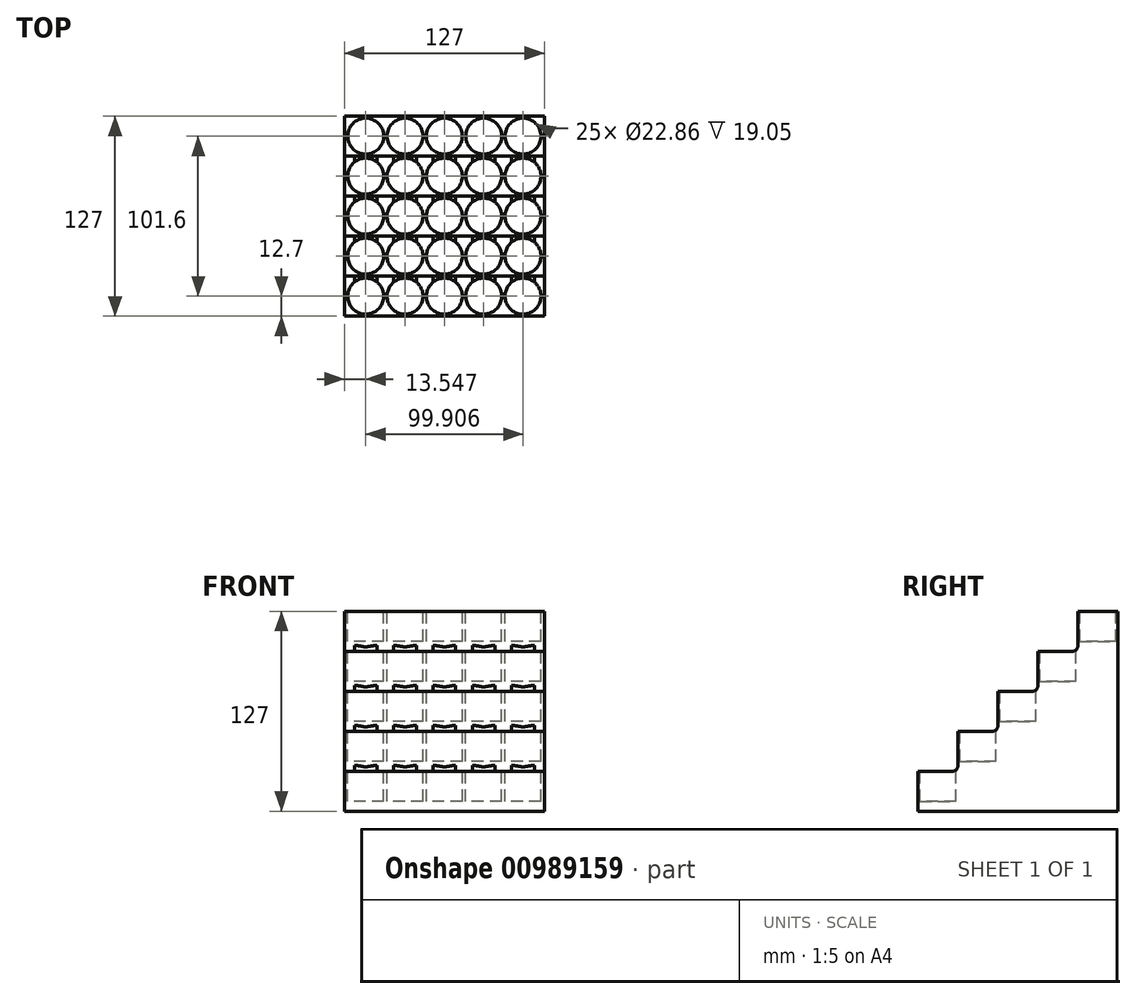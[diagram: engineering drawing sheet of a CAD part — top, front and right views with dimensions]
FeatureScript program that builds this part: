
annotation { "Feature Type Name" : "Feature", "Feature Type Description" : "" }
export const myFeature = defineFeature(function(context is Context, id is Id, definition is map)
    precondition{}
    {
        {
            var Q0;
            Q0=qCreatedBy(makeId("Top.planeOp"),FACE);
            var sketch = newSketch(context, id + "F0", { "sketchPlane" : qUnion([Q0])});
            skLineSegment(sketch, "E0.bottom", {"start": v(63.5, -63.5) * mm, "end": v(-63.5, -63.5) * mm});
            skLineSegment(sketch, "E0.top", {"start": v(63.5, 63.5) * mm, "end": v(-63.5, 63.5) * mm});
            skLineSegment(sketch, "E0.left", {"start": v(63.5, -63.5) * mm, "end": v(63.5, 63.5) * mm});
            skLineSegment(sketch, "E0.right", {"start": v(-63.5, -63.5) * mm, "end": v(-63.5, 63.5) * mm});
            skPoint(sketch, "E0.middle", {"position": v(0, 0) * mm});
            skSolve(sketch);
        }
        {
            var Q0;
            Q0=makeQuery(id+"F0.imprint","IMPRINT",FACE,{"disambiguationData":[TD([[makeQuery(id+"F0.imprint","IMPRINT",EDGE,{"derivedFrom":sQuery(id+"F0.wireOp",EDGE,"E0.bottom")}),-1.0]])]});
            extrude(context, id + "F1", {"entities" : qUnion([Q0]), "endBound" : BoundingType.SYMMETRIC, "depth" : 127 * mm, "offsetDistance" : 25.4 * mm});
        }
        {
            var Q0;
            Q0=makeQuery(id+"F1.opExtrude","CAP_FACE",FACE,{"disambiguationData":[OSD([sQuery(id+"F0.wireOp",EDGE,"E0.bottom"),sQuery(id+"F0.wireOp",EDGE,"E0.top"),sQuery(id+"F0.wireOp",EDGE,"E0.left"),sQuery(id+"F0.wireOp",EDGE,"E0.right")])],"isStart":false});
            var sketch = newSketch(context, id + "F2", { "sketchPlane" : qUnion([Q0])});
            skLineSegment(sketch, "E1.bottom", {"start": v(-63.5, -63.5) * mm, "end": v(63.5, -63.5) * mm});
            skLineSegment(sketch, "E1.top", {"start": v(-63.5, -38.1) * mm, "end": v(63.5, -38.1) * mm});
            skLineSegment(sketch, "E1.left", {"start": v(-63.5, -63.5) * mm, "end": v(-63.5, -38.1) * mm});
            skLineSegment(sketch, "E1.right", {"start": v(63.5, -63.5) * mm, "end": v(63.5, -38.1) * mm});
            skSolve(sketch);
        }
        {
            var Q0;
            Q0=makeQuery(id+"F2.imprint","IMPRINT",FACE,{"disambiguationData":[TD([[makeQuery(id+"F2.imprint","IMPRINT",EDGE,{"derivedFrom":sQuery(id+"F2.wireOp",EDGE,"E1.bottom")}),-1.0]])]});
            extrude(context, id + "F3", {"entities" : qUnion([Q0]), "operationType" : NewBodyOperationType.REMOVE, "oppositeDirection" : true, "depth" : 101.6 * mm, "offsetDistance" : 25.4 * mm});
        }
        {
            var Q0;
            Q0=makeQuery(id+"F1.opExtrude","CAP_FACE",FACE,{"disambiguationData":[OSD([sQuery(id+"F0.wireOp",EDGE,"E0.bottom"),sQuery(id+"F0.wireOp",EDGE,"E0.top"),sQuery(id+"F0.wireOp",EDGE,"E0.left"),sQuery(id+"F0.wireOp",EDGE,"E0.right")])],"isStart":false});
            var sketch = newSketch(context, id + "F4", { "sketchPlane" : qUnion([Q0])});
            skLineSegment(sketch, "E2.bottom", {"start": v(-63.5, -38.1) * mm, "end": v(63.5, -38.1) * mm});
            skLineSegment(sketch, "E2.top", {"start": v(-63.5, -12.7) * mm, "end": v(63.5, -12.7) * mm});
            skLineSegment(sketch, "E2.left", {"start": v(-63.5, -38.1) * mm, "end": v(-63.5, -12.7) * mm});
            skLineSegment(sketch, "E2.right", {"start": v(63.5, -38.1) * mm, "end": v(63.5, -12.7) * mm});
            skSolve(sketch);
        }
        {
            var Q0;
            Q0=makeQuery(id+"F4.imprint","IMPRINT",FACE,{"disambiguationData":[TD([[makeQuery(id+"F4.imprint","IMPRINT",EDGE,{"derivedFrom":sQuery(id+"F4.wireOp",EDGE,"E2.bottom")}),1.0]])]});
            extrude(context, id + "F5", {"entities" : qUnion([Q0]), "operationType" : NewBodyOperationType.REMOVE, "oppositeDirection" : true, "depth" : 76.2 * mm, "offsetDistance" : 25.4 * mm});
        }
        {
            var Q0;
            Q0=makeQuery(id+"F1.opExtrude","CAP_FACE",FACE,{"disambiguationData":[OSD([sQuery(id+"F0.wireOp",EDGE,"E0.bottom"),sQuery(id+"F0.wireOp",EDGE,"E0.top"),sQuery(id+"F0.wireOp",EDGE,"E0.left"),sQuery(id+"F0.wireOp",EDGE,"E0.right")])],"isStart":false});
            var sketch = newSketch(context, id + "F6", { "sketchPlane" : qUnion([Q0])});
            skLineSegment(sketch, "E3.bottom", {"start": v(-63.5, -12.7) * mm, "end": v(63.5, -12.7) * mm});
            skLineSegment(sketch, "E3.top", {"start": v(-63.5, 12.7) * mm, "end": v(63.5, 12.7) * mm});
            skLineSegment(sketch, "E3.left", {"start": v(-63.5, -12.7) * mm, "end": v(-63.5, 12.7) * mm});
            skLineSegment(sketch, "E3.right", {"start": v(63.5, -12.7) * mm, "end": v(63.5, 12.7) * mm});
            skSolve(sketch);
        }
        {
            var Q0;
            Q0=makeQuery(id+"F6.imprint","IMPRINT",FACE,{"disambiguationData":[TD([[makeQuery(id+"F6.imprint","IMPRINT",EDGE,{"derivedFrom":sQuery(id+"F6.wireOp",EDGE,"E3.bottom")}),1.0]])]});
            extrude(context, id + "F7", {"entities" : qUnion([Q0]), "operationType" : NewBodyOperationType.REMOVE, "oppositeDirection" : true, "depth" : 50.8 * mm, "offsetDistance" : 25.4 * mm});
        }
        {
            var Q0;
            Q0=makeQuery(id+"F1.opExtrude","CAP_FACE",FACE,{"disambiguationData":[OSD([sQuery(id+"F0.wireOp",EDGE,"E0.bottom"),sQuery(id+"F0.wireOp",EDGE,"E0.top"),sQuery(id+"F0.wireOp",EDGE,"E0.left"),sQuery(id+"F0.wireOp",EDGE,"E0.right")])],"isStart":false});
            var sketch = newSketch(context, id + "F8", { "sketchPlane" : qUnion([Q0])});
            skLineSegment(sketch, "E4.bottom", {"start": v(-63.5, 12.7) * mm, "end": v(63.5, 12.7) * mm});
            skLineSegment(sketch, "E4.top", {"start": v(-63.5, 38.1) * mm, "end": v(63.5, 38.1) * mm});
            skLineSegment(sketch, "E4.left", {"start": v(-63.5, 12.7) * mm, "end": v(-63.5, 38.1) * mm});
            skLineSegment(sketch, "E4.right", {"start": v(63.5, 12.7) * mm, "end": v(63.5, 38.1) * mm});
            skSolve(sketch);
        }
        {
            var Q0;
            Q0=makeQuery(id+"F8.imprint","IMPRINT",FACE,{"disambiguationData":[TD([[makeQuery(id+"F8.imprint","IMPRINT",EDGE,{"derivedFrom":sQuery(id+"F8.wireOp",EDGE,"E4.bottom")}),1.0]])]});
            extrude(context, id + "F9", {"entities" : qUnion([Q0]), "operationType" : NewBodyOperationType.REMOVE, "oppositeDirection" : true, "depth" : 25.4 * mm, "offsetDistance" : 25.4 * mm});
        }
        {
            var Q0;
            Q0=makeQuery(id+"F1.opExtrude","CAP_FACE",FACE,{"disambiguationData":[OSD([sQuery(id+"F0.wireOp",EDGE,"E0.bottom"),sQuery(id+"F0.wireOp",EDGE,"E0.top"),sQuery(id+"F0.wireOp",EDGE,"E0.left"),sQuery(id+"F0.wireOp",EDGE,"E0.right")])],"isStart":false});
            var sketch = newSketch(context, id + "F10", { "sketchPlane" : qUnion([Q0])});
            skLineSegment(sketch, "E5", {"start": v(-63.5, 50.8) * mm, "end": v(0, 50.8) * mm, "construction": true});
            skLineSegment(sketch, "E6", {"start": v(0, 50.8) * mm, "end": v(63.5, 50.8) * mm, "construction": true});
            skSolve(sketch);
        }
        {
            var Q0;
            Q0=makeQuery(id+"F10.imprint","IMPRINT",FACE,{"disambiguationData":[TD([[makeQuery(id+"F10.imprint","IMPRINT",EDGE,{"derivedFrom":makeQuery(id+"F1.opExtrude","CAP_EDGE",EDGE,{"disambiguationData":[OSD([sQuery(id+"F0.wireOp",EDGE,"E0.top")])],"isStart":false})}),1.0]])]});
            var sketch = newSketch(context, id + "F11", { "sketchPlane" : qUnion([Q0])});
            skCircle(sketch, "E7", {"center": v(0, 50.8) * mm, "radius": 11.43 * mm});
            skCircle(sketch, "E8", {"center": v(-24.98, 50.8) * mm, "radius": 11.43 * mm});
            skCircle(sketch, "E9", {"center": v(24.98, 50.8) * mm, "radius": 11.43 * mm});
            skCircle(sketch, "E10", {"center": v(49.95, 50.8) * mm, "radius": 11.43 * mm});
            skCircle(sketch, "E11", {"center": v(-49.95, 50.8) * mm, "radius": 11.43 * mm});
            skSolve(sketch);
        }
        {
            var Q0;
            Q0 = qSketchRegion(id + "F11", true);
            extrude(context, id + "F12", {"entities" : qUnion([Q0]), "operationType" : NewBodyOperationType.REMOVE, "oppositeDirection" : true, "depth" : 19.05 * mm, "offsetDistance" : 25.4 * mm});
        }
        {
            var Q0;
            Q0=makeQuery(id+"F9.boolean.opBoolean","COPY",FACE,{"derivedFrom":makeQuery(id+"F9.opExtrude","CAP_FACE",FACE,{"disambiguationData":[OSD([sQuery(id+"F8.wireOp",EDGE,"E4.bottom"),sQuery(id+"F8.wireOp",EDGE,"E4.top"),sQuery(id+"F8.wireOp",EDGE,"E4.left"),sQuery(id+"F8.wireOp",EDGE,"E4.right")])],"isStart":false})});
            var sketch = newSketch(context, id + "F13", { "sketchPlane" : qUnion([Q0])});
            skCircle(sketch, "E12", {"center": v(0, 25.4) * mm, "radius": 11.43 * mm});
            skCircle(sketch, "E13", {"center": v(-24.98, 25.4) * mm, "radius": 11.43 * mm});
            skCircle(sketch, "E14", {"center": v(24.98, 25.4) * mm, "radius": 11.43 * mm});
            skCircle(sketch, "E15", {"center": v(49.95, 25.4) * mm, "radius": 11.43 * mm});
            skCircle(sketch, "E16", {"center": v(-49.95, 25.4) * mm, "radius": 11.43 * mm});
            skLineSegment(sketch, "E17", {"start": v(-63.5, 25.4) * mm, "end": v(0, 25.4) * mm, "construction": true});
            skSolve(sketch);
        }
        {
            var Q0;
            Q0 = qSketchRegion(id + "F13", true);
            extrude(context, id + "F14", {"entities" : qUnion([Q0]), "operationType" : NewBodyOperationType.REMOVE, "oppositeDirection" : true, "depth" : 19.05 * mm, "offsetDistance" : 25.4 * mm});
        }
        {
            var Q0;
            Q0=makeQuery(id+"F7.boolean.opBoolean","COPY",FACE,{"derivedFrom":makeQuery(id+"F7.opExtrude","CAP_FACE",FACE,{"disambiguationData":[OSD([sQuery(id+"F6.wireOp",EDGE,"E3.bottom"),sQuery(id+"F6.wireOp",EDGE,"E3.top"),sQuery(id+"F6.wireOp",EDGE,"E3.left"),sQuery(id+"F6.wireOp",EDGE,"E3.right")])],"isStart":false})});
            var sketch = newSketch(context, id + "F15", { "sketchPlane" : qUnion([Q0])});
            skLineSegment(sketch, "E18", {"start": v(0, 0) * mm, "end": v(-63.5, 0) * mm, "construction": true});
            skCircle(sketch, "E19", {"center": v(0, 0) * mm, "radius": 11.43 * mm});
            skCircle(sketch, "E20", {"center": v(-24.98, 0) * mm, "radius": 11.43 * mm});
            skCircle(sketch, "E21", {"center": v(24.98, 0) * mm, "radius": 11.43 * mm});
            skCircle(sketch, "E22", {"center": v(49.95, 0) * mm, "radius": 11.43 * mm});
            skCircle(sketch, "E23", {"center": v(-49.95, 0) * mm, "radius": 11.43 * mm});
            skSolve(sketch);
        }
        {
            var Q0;
            Q0 = qSketchRegion(id + "F15", true);
            extrude(context, id + "F16", {"entities" : qUnion([Q0]), "operationType" : NewBodyOperationType.REMOVE, "oppositeDirection" : true, "depth" : 19.05 * mm, "offsetDistance" : 25.4 * mm});
        }
        {
            var Q0;
            Q0=makeQuery(id+"F3.boolean.opBoolean","COPY",FACE,{"derivedFrom":makeQuery(id+"F3.opExtrude","CAP_FACE",FACE,{"disambiguationData":[OSD([sQuery(id+"F2.wireOp",EDGE,"E1.bottom"),sQuery(id+"F2.wireOp",EDGE,"E1.top"),sQuery(id+"F2.wireOp",EDGE,"E1.left"),sQuery(id+"F2.wireOp",EDGE,"E1.right")])],"isStart":false})});
            var sketch = newSketch(context, id + "F17", { "sketchPlane" : qUnion([Q0])});
            skLineSegment(sketch, "E24", {"start": v(-63.5, -50.8) * mm, "end": v(0, -50.8) * mm, "construction": true});
            skPoint(sketch, "E24.endSnap0", {"position": v(0, -38.1) * mm});
            skCircle(sketch, "E25", {"center": v(0, -50.8) * mm, "radius": 11.43 * mm});
            skCircle(sketch, "E26", {"center": v(-24.98, -50.8) * mm, "radius": 11.43 * mm});
            skCircle(sketch, "E27", {"center": v(24.98, -50.8) * mm, "radius": 11.43 * mm});
            skCircle(sketch, "E28", {"center": v(49.95, -50.8) * mm, "radius": 11.43 * mm});
            skCircle(sketch, "E29", {"center": v(-49.95, -50.8) * mm, "radius": 11.43 * mm});
            skSolve(sketch);
        }
        {
            var Q0;
            Q0 = qSketchRegion(id + "F17", true);
            extrude(context, id + "F18", {"entities" : qUnion([Q0]), "operationType" : NewBodyOperationType.REMOVE, "oppositeDirection" : true, "depth" : 19.05 * mm, "offsetDistance" : 25.4 * mm});
        }
        {
            var Q0;
            Q0=makeQuery(id+"F5.boolean.opBoolean","COPY",FACE,{"derivedFrom":makeQuery(id+"F5.opExtrude","CAP_FACE",FACE,{"disambiguationData":[OSD([sQuery(id+"F4.wireOp",EDGE,"E2.bottom"),sQuery(id+"F4.wireOp",EDGE,"E2.top"),sQuery(id+"F4.wireOp",EDGE,"E2.left"),sQuery(id+"F4.wireOp",EDGE,"E2.right")])],"isStart":false})});
            var sketch = newSketch(context, id + "F19", { "sketchPlane" : qUnion([Q0])});
            skLineSegment(sketch, "E30", {"start": v(-63.5, -25.4) * mm, "end": v(0, -25.4) * mm, "construction": true});
            skCircle(sketch, "E31", {"center": v(0, -25.4) * mm, "radius": 11.43 * mm});
            skCircle(sketch, "E32", {"center": v(-24.98, -25.4) * mm, "radius": 11.43 * mm});
            skCircle(sketch, "E33", {"center": v(24.98, -25.4) * mm, "radius": 11.43 * mm});
            skCircle(sketch, "E34", {"center": v(49.95, -25.4) * mm, "radius": 11.43 * mm});
            skCircle(sketch, "E35", {"center": v(-49.95, -25.4) * mm, "radius": 11.43 * mm});
            skSolve(sketch);
        }
        {
            var Q0;
            Q0 = qSketchRegion(id + "F19", true);
            extrude(context, id + "F20", {"entities" : qUnion([Q0]), "operationType" : NewBodyOperationType.REMOVE, "oppositeDirection" : true, "depth" : 19.05 * mm, "offsetDistance" : 25.4 * mm});
        }
        {
            var Q0;
            Q0=makeQuery(id+"F3.boolean.opBoolean","COPY",EDGE,{"derivedFrom":makeQuery(id+"F3.opExtrude","CAP_EDGE",EDGE,{"disambiguationData":[OSD([sQuery(id+"F2.wireOp",EDGE,"E1.bottom")])],"isStart":false})});
            var Q1;
            Q1=makeQuery(id+"F5.boolean.opBoolean","COPY",EDGE,{"derivedFrom":makeQuery(id+"F5.opExtrude","CAP_EDGE",EDGE,{"disambiguationData":[OSD([sQuery(id+"F4.wireOp",EDGE,"E2.bottom")])],"isStart":false})});
            var Q2;
            Q2=makeQuery(id+"F7.boolean.opBoolean","COPY",EDGE,{"derivedFrom":makeQuery(id+"F7.opExtrude","CAP_EDGE",EDGE,{"disambiguationData":[OSD([sQuery(id+"F6.wireOp",EDGE,"E3.bottom")])],"isStart":false})});
            var Q3;
            Q3=makeQuery(id+"F9.boolean.opBoolean","COPY",EDGE,{"derivedFrom":makeQuery(id+"F9.opExtrude","CAP_EDGE",EDGE,{"disambiguationData":[OSD([sQuery(id+"F8.wireOp",EDGE,"E4.bottom")])],"isStart":false})});
            var Q4;
            Q4=makeQuery(id+"F9.boolean.opBoolean","COPY",EDGE,{"derivedFrom":makeQuery(id+"F9.opExtrude","CAP_EDGE",EDGE,{"disambiguationData":[OSD([sQuery(id+"F8.wireOp",EDGE,"E4.top")])],"isStart":true})});
            var Q5;
            Q5=makeQuery(id+"F9.boolean.opBoolean","COPY",EDGE,{"derivedFrom":makeQuery(id+"F9.opExtrude","CAP_EDGE",EDGE,{"disambiguationData":[OSD([sQuery(id+"F8.wireOp",EDGE,"E4.top")])],"isStart":false})});
            var Q6;
            Q6=makeQuery(id+"F7.boolean.opBoolean","COPY",EDGE,{"derivedFrom":makeQuery(id+"F7.opExtrude","CAP_EDGE",EDGE,{"disambiguationData":[OSD([sQuery(id+"F6.wireOp",EDGE,"E3.top")])],"isStart":false})});
            var Q7;
            Q7=makeQuery(id+"F5.boolean.opBoolean","COPY",EDGE,{"derivedFrom":makeQuery(id+"F5.opExtrude","CAP_EDGE",EDGE,{"disambiguationData":[OSD([sQuery(id+"F4.wireOp",EDGE,"E2.top")])],"isStart":false})});
            var Q8;
            Q8=makeQuery(id+"F3.boolean.opBoolean","COPY",EDGE,{"derivedFrom":makeQuery(id+"F3.opExtrude","CAP_EDGE",EDGE,{"disambiguationData":[OSD([sQuery(id+"F2.wireOp",EDGE,"E1.top")])],"isStart":false})});
            fillet(context, id + "F21", {"entities" : qUnion([Q0, Q1, Q2, Q3, Q4, Q5, Q6, Q7, Q8]), "radius" : 3.8 * mm, "tangentPropagation" : true, "allowEdgeOverflow" : false});
        }
    });
